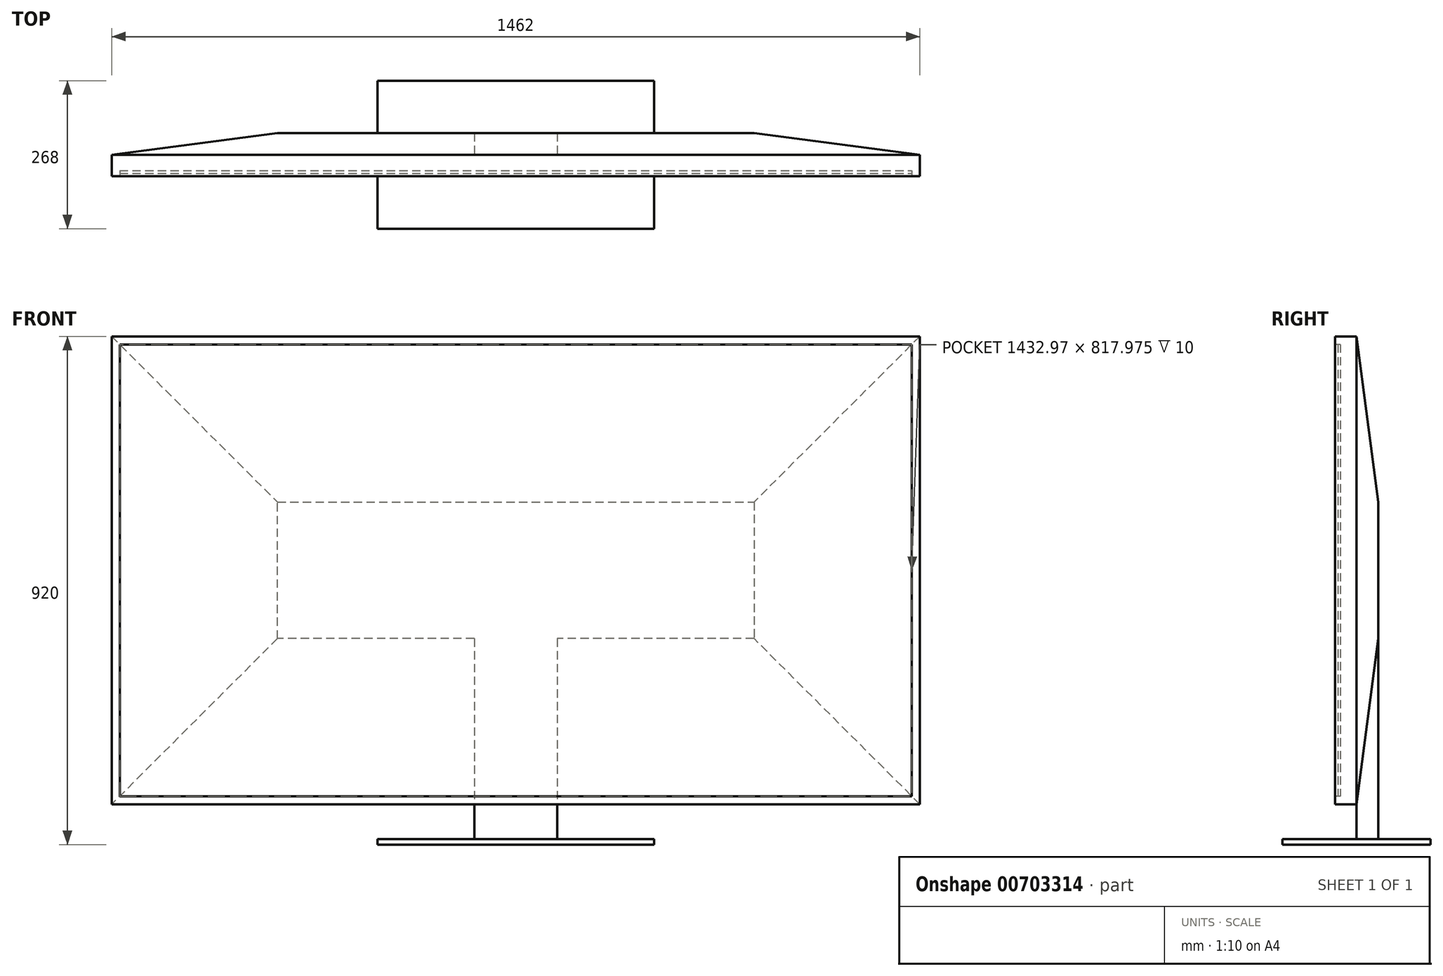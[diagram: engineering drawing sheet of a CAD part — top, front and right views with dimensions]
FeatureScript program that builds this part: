
annotation { "Feature Type Name" : "Feature", "Feature Type Description" : "" }
export const myFeature = defineFeature(function(context is Context, id is Id, definition is map)
    precondition{}
    {
        {
            var Q0;
            Q0=qCreatedBy(makeId("Front.planeOp"),FACE);
            var sketch = newSketch(context, id + "F0", { "sketchPlane" : qUnion([Q0])});
            skLineSegment(sketch, "E0.bottom", {"start": v(-731, 920) * mm, "end": v(731, 920) * mm});
            skLineSegment(sketch, "E0.top", {"start": v(-731, 73) * mm, "end": v(731, 73) * mm});
            skLineSegment(sketch, "E0.left", {"start": v(-731, 920) * mm, "end": v(-731, 73) * mm});
            skLineSegment(sketch, "E0.right", {"start": v(731, 920) * mm, "end": v(731, 73) * mm});
            skLineSegment(sketch, "E1", {"start": v(0, 73) * mm, "end": v(0, 0) * mm});
            skLineSegment(sketch, "E2.bottom", {"start": v(-716.49, 905.49) * mm, "end": v(716.49, 905.49) * mm});
            skLineSegment(sketch, "E2.top", {"start": v(-716.49, 87.51) * mm, "end": v(716.49, 87.51) * mm});
            skLineSegment(sketch, "E2.left", {"start": v(-716.49, 905.49) * mm, "end": v(-716.49, 87.51) * mm});
            skLineSegment(sketch, "E2.right", {"start": v(716.49, 905.49) * mm, "end": v(716.49, 87.51) * mm});
            skLineSegment(sketch, "E3", {"start": v(0, 905.49) * mm, "end": v(0, 920) * mm});
            skLineSegment(sketch, "E4", {"start": v(-716.49, 496.5) * mm, "end": v(-731, 496.5) * mm});
            skSolve(sketch);
        }
        {
            var Q0;
            Q0=qCreatedBy(makeId("Right.planeOp"),FACE);
            var sketch = newSketch(context, id + "F1", { "sketchPlane" : qUnion([Q0])});
            skLineSegment(sketch, "E5.bottom", {"start": v(78, 920) * mm, "end": v(0, 920) * mm});
            skLineSegment(sketch, "E5.top", {"start": v(78, 73) * mm, "end": v(0, 73) * mm});
            skLineSegment(sketch, "E5.left", {"start": v(78, 920) * mm, "end": v(78, 73) * mm});
            skLineSegment(sketch, "E5.right", {"start": v(0, 920) * mm, "end": v(0, 73) * mm});
            skLineSegment(sketch, "E6.top", {"start": v(173, 0) * mm, "end": v(-95, 0) * mm});
            skLineSegment(sketch, "E6.left", {"start": v(173, 10) * mm, "end": v(173, 0) * mm});
            skLineSegment(sketch, "E6.right", {"start": v(-95, 10) * mm, "end": v(-95, 0) * mm});
            skLineSegment(sketch, "E7", {"start": v(39, 496.5) * mm, "end": v(78, 496.5) * mm});
            skLineSegment(sketch, "E8", {"start": v(78, 496.5) * mm, "end": v(78, 10) * mm});
            skLineSegment(sketch, "E9", {"start": v(39, 496.5) * mm, "end": v(39, 73) * mm});
            skLineSegment(sketch, "E10", {"start": v(39, 73) * mm, "end": v(39, 10) * mm});
            skLineSegment(sketch, "E11", {"start": v(173, 10) * mm, "end": v(-95, 10) * mm});
            skSolve(sketch);
        }
        {
            var Q0;
            {var subQ3=sQuery(id+"F0.wireOp",EDGE,"E3");Q0=makeQuery(id+"F0.imprint","IMPRINT",FACE,{"disambiguationData":[TD([[makeQuery(id+"F0.imprint","IMPRINT",EDGE,{"derivedFrom":subQ3}),1.0]])]});}
            var Q1;
            {var subQ6=sQuery(id+"F0.wireOp",EDGE,"E0.right");Q1=makeQuery(id+"F0.imprint","IMPRINT",FACE,{"disambiguationData":[TD([[makeQuery(id+"F0.imprint","IMPRINT",EDGE,{"derivedFrom":subQ6}),-1.0]])]});}
            var Q2;
            {var subQ4=sQuery(id+"F0.wireOp",EDGE,"E2.top");Q2=makeQuery(id+"F0.imprint","IMPRINT",FACE,{"disambiguationData":[TD([[makeQuery(id+"F0.imprint","IMPRINT",EDGE,{"derivedFrom":subQ4}),1.0]])]});}
            extrude(context, id + "F2", {"entities" : qUnion([Q0, Q1, Q2]), "oppositeDirection" : true, "depth" : 78 * mm, "offsetDistance" : 25 * mm});
        }
        {
            var Q0;
            {var subQ4=sQuery(id+"F0.wireOp",EDGE,"E2.top");Q0=makeQuery(id+"F0.imprint","IMPRINT",FACE,{"disambiguationData":[TD([[makeQuery(id+"F0.imprint","IMPRINT",EDGE,{"derivedFrom":subQ4}),1.0]])]});}
            extrude(context, id + "F3", {"entities" : qUnion([Q0]), "operationType" : NewBodyOperationType.REMOVE, "oppositeDirection" : true, "depth" : 10 * mm, "offsetDistance" : 25 * mm});
        }
        {
            var Q0;
            {var subQ4=sQuery(id+"F0.wireOp",EDGE,"E2.top");Q0=makeQuery(id+"F0.imprint","IMPRINT",FACE,{"disambiguationData":[TD([[makeQuery(id+"F0.imprint","IMPRINT",EDGE,{"derivedFrom":subQ4}),1.0]])]});}
            extrude(context, id + "F4", {"entities" : qUnion([Q0]), "oppositeDirection" : true, "depth" : 10 * mm, "offsetDistance" : 25 * mm, "hasSecondDirection" : true, "secondDirectionOppositeDirection" : true, "secondDirectionDepth" : 5 * mm});
        }
        {
            var Q0;
            Q0=makeQuery(id+"F2.opExtrude","CAP_EDGE",EDGE,{"disambiguationData":[OSD([sQuery(id+"F0.wireOp",EDGE,"E0.bottom")])],"isStart":false});
            var Q1;
            Q1=makeQuery(id+"F2.opExtrude","CAP_EDGE",EDGE,{"disambiguationData":[OSD([sQuery(id+"F0.wireOp",EDGE,"E0.left")])],"isStart":false});
            var Q2;
            Q2=makeQuery(id+"F2.opExtrude","CAP_EDGE",EDGE,{"disambiguationData":[OSD([sQuery(id+"F0.wireOp",EDGE,"E0.top")])],"isStart":false});
            var Q3;
            Q3=makeQuery(id+"F2.opExtrude","CAP_EDGE",EDGE,{"disambiguationData":[OSD([sQuery(id+"F0.wireOp",EDGE,"E0.right")])],"isStart":false});
            chamfer(context, id + "F5", {"entities" : qUnion([Q0, Q1, Q2, Q3]), "chamferType" : ChamferType.TWO_OFFSETS, "width1" : 300 * mm, "oppositeDirection" : false, "width2" : 39 * mm, "tangentPropagation" : true});
        }
        {
            var Q0;
            Q0=makeQuery(id+"F1.imprint","IMPRINT",FACE,{"disambiguationData":[TD([[makeQuery(id+"F1.imprint","IMPRINT",EDGE,{"derivedFrom":sQuery(id+"F1.wireOp",EDGE,"E6.top")}),-1.0]])]});
            extrude(context, id + "F6", {"entities" : qUnion([Q0]), "depth" : 250 * mm, "offsetDistance" : 25 * mm, "hasSecondDirection" : true, "secondDirectionOppositeDirection" : true, "secondDirectionDepth" : 250 * mm});
        }
        {
            var Q0;
            {var subQ4=sQuery(id+"F1.wireOp",EDGE,"E7");Q0=makeQuery(id+"F1.imprint","IMPRINT",FACE,{"disambiguationData":[TD([[makeQuery(id+"F1.imprint","IMPRINT",EDGE,{"derivedFrom":subQ4}),-1.0]])]});}
            var Q1;
            {var subQ3=sQuery(id+"F1.wireOp",EDGE,"E10");Q1=makeQuery(id+"F1.imprint","IMPRINT",FACE,{"disambiguationData":[TD([[makeQuery(id+"F1.imprint","IMPRINT",EDGE,{"derivedFrom":subQ3}),1.0]])]});}
            extrude(context, id + "F7", {"entities" : qUnion([Q0, Q1]), "operationType" : NewBodyOperationType.ADD, "depth" : 75 * mm, "offsetDistance" : 25 * mm, "hasSecondDirection" : true, "secondDirectionOppositeDirection" : true, "secondDirectionDepth" : 75 * mm});
        }
    });
